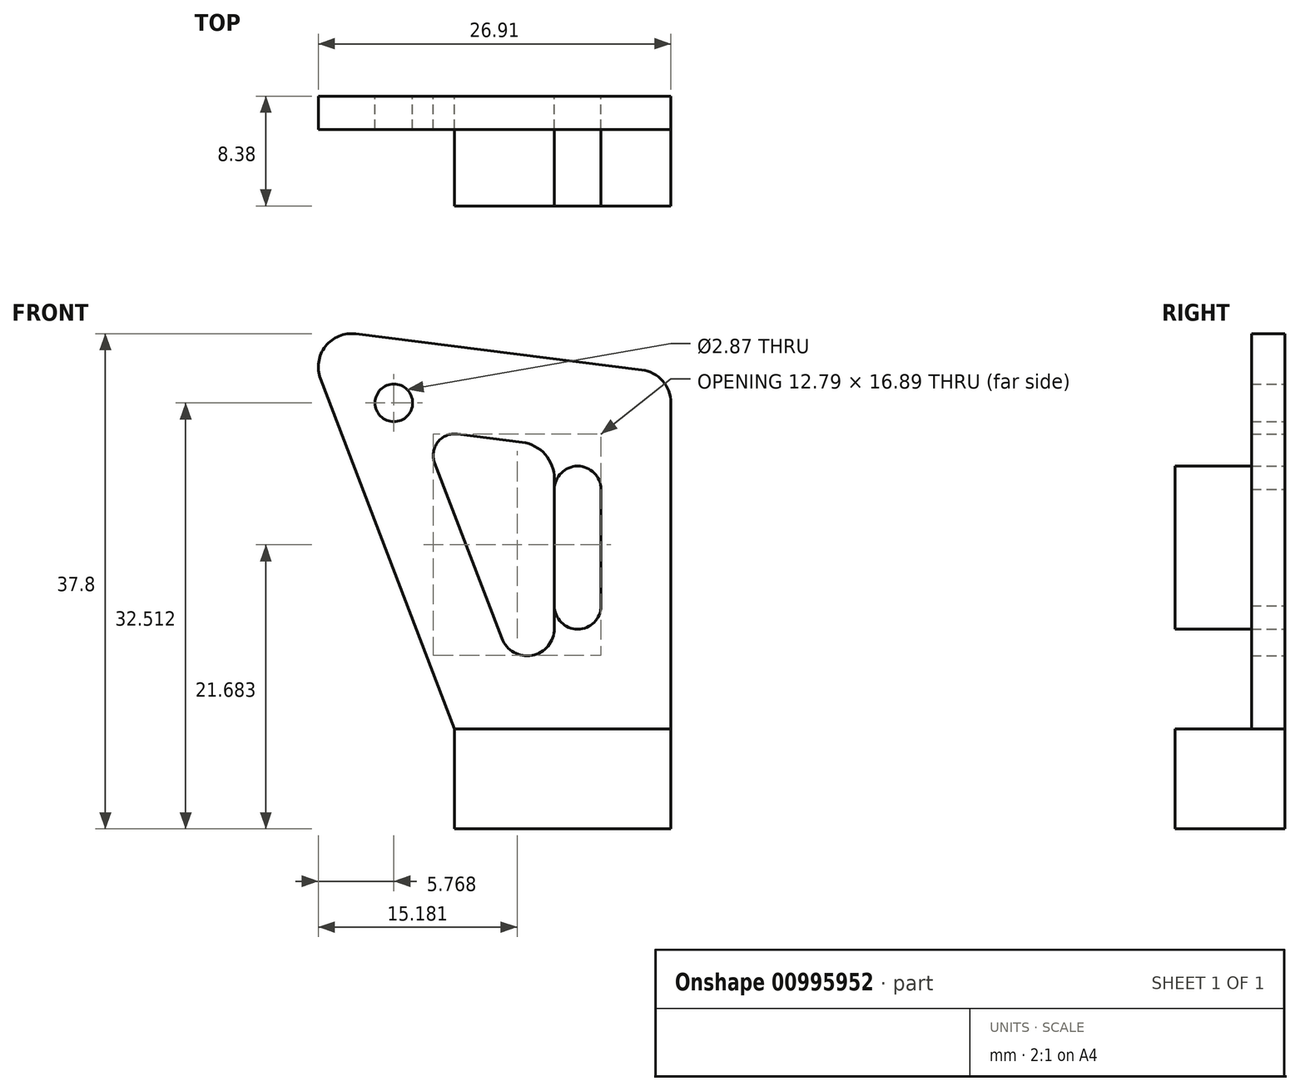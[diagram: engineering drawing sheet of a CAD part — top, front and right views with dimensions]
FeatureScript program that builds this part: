
annotation { "Feature Type Name" : "Feature", "Feature Type Description" : "" }
export const myFeature = defineFeature(function(context is Context, id is Id, definition is map)
    precondition{}
    {
        {
            var Q0;
            Q0=qCreatedBy(makeId("Front.planeOp"),FACE);
            var sketch = newSketch(context, id + "F0", { "sketchPlane" : qUnion([Q0])});
            skLineSegment(sketch, "E0", {"start": v(-2.8, 0.18) * mm, "end": v(-12.25, 24.9) * mm, "construction": true});
            skLineSegment(sketch, "E1", {"start": v(-7.62, 0) * mm, "end": v(8.9, 0) * mm});
            skCircle(sketch, "E2", {"center": v(-12.25, 24.9) * mm, "radius": 1.44 * mm});
            skLineSegment(sketch, "E3", {"start": v(-7.62, 0) * mm, "end": v(-17.85, 26.73) * mm});
            skArc(sketch, "E4", {"start": v(-17.85, 26.73) * mm, "mid": v(-17.48, 29.2) * mm, "end": v(-15.16, 30.16) * mm});
            skLineSegment(sketch, "E5", {"start": v(-15.16, 30.16) * mm, "end": v(6.67, 27.41) * mm});
            skArc(sketch, "E6", {"start": v(6.67, 27.41) * mm, "mid": v(8.25, 26.57) * mm, "end": v(8.89, 24.9) * mm});
            skLineSegment(sketch, "E7", {"start": v(8.9, 0) * mm, "end": v(8.89, 24.9) * mm});
            skLineSegment(sketch, "E8", {"start": v(3.56, 18.29) * mm, "end": v(3.56, 9.4) * mm});
            skLineSegment(sketch, "E9", {"start": v(0, 18.29) * mm, "end": v(0, 9.4) * mm});
            skArc(sketch, "E10", {"start": v(0, 18.29) * mm, "mid": v(1.78, 20.07) * mm, "end": v(3.56, 18.29) * mm});
            skArc(sketch, "E11", {"start": v(0, 9.4) * mm, "mid": v(1.78, 7.62) * mm, "end": v(3.56, 9.4) * mm});
            skLineSegment(sketch, "E12", {"start": v(-4.01, 6.92) * mm, "end": v(-9.14, 20.3) * mm});
            skArc(sketch, "E13", {"start": v(-9.14, 20.3) * mm, "mid": v(-8.9, 21.9) * mm, "end": v(-7.4, 22.51) * mm});
            skLineSegment(sketch, "E14", {"start": v(-7.4, 22.51) * mm, "end": v(-2.47, 21.89) * mm});
            skLineSegment(sketch, "E15", {"start": v(0, 19.1) * mm, "end": v(0, 7.66) * mm});
            skArc(sketch, "E16", {"start": v(-2.47, 21.89) * mm, "mid": v(-0.7, 20.96) * mm, "end": v(0, 19.1) * mm});
            skArc(sketch, "E17", {"start": v(-4.01, 6.92) * mm, "mid": v(-1.7, 5.62) * mm, "end": v(0, 7.66) * mm});
            skLineSegment(sketch, "E18", {"start": v(-17.15, 24.9) * mm, "end": v(8.89, 24.9) * mm, "construction": true});
            skSolve(sketch);
        }
        {
            var Q0;
            Q0=qCreatedBy(makeId("Front.planeOp"),FACE);
            var sketch = newSketch(context, id + "F1", { "sketchPlane" : qUnion([Q0])});
            skLineSegment(sketch, "E19", {"start": v(0, 0) * mm, "end": v(0, -76.2) * mm, "construction": true});
            skLineSegment(sketch, "E20", {"start": v(-12.7, -76.2) * mm, "end": v(12.7, -76.2) * mm});
            skLineSegment(sketch, "E21", {"start": v(-7.62, 0) * mm, "end": v(8.9, 0) * mm});
            skLineSegment(sketch, "E22", {"start": v(-7.62, -7.62) * mm, "end": v(8.9, -7.62) * mm});
            skLineSegment(sketch, "E23", {"start": v(-7.62, 0) * mm, "end": v(-7.62, -7.62) * mm});
            skLineSegment(sketch, "E24", {"start": v(8.9, 0) * mm, "end": v(8.9, -7.62) * mm});
            skLineSegment(sketch, "E25", {"start": v(-7.62, -7.62) * mm, "end": v(-25.4, -63.5) * mm});
            skLineSegment(sketch, "E26", {"start": v(8.89, -7.62) * mm, "end": v(25.4, -63.5) * mm});
            skArc(sketch, "E27", {"start": v(-12.7, -76.2) * mm, "mid": v(-21.68, -72.48) * mm, "end": v(-25.4, -63.5) * mm});
            skArc(sketch, "E28", {"start": v(12.7, -76.2) * mm, "mid": v(21.68, -72.48) * mm, "end": v(25.4, -63.5) * mm});
            skArc(sketch, "E29.0.startCap", {"start": v(-10.16, -68.58) * mm, "mid": v(-16.5, -62.23) * mm, "end": v(-10.16, -55.88) * mm});
            skArc(sketch, "E29.0.endCap", {"start": v(10.16, -55.88) * mm, "mid": v(16.51, -62.23) * mm, "end": v(10.16, -68.58) * mm});
            skLineSegment(sketch, "E29.0.left", {"start": v(-10.16, -55.88) * mm, "end": v(10.16, -55.88) * mm});
            skLineSegment(sketch, "E29.0.right", {"start": v(-10.16, -68.58) * mm, "end": v(10.16, -68.58) * mm});
            skArc(sketch, "E30.0.startCap", {"start": v(-5.08, -48.26) * mm, "mid": v(-11.43, -41.9) * mm, "end": v(-5.08, -35.56) * mm});
            skArc(sketch, "E30.0.endCap", {"start": v(5.08, -35.56) * mm, "mid": v(11.43, -41.9) * mm, "end": v(5.08, -48.26) * mm});
            skLineSegment(sketch, "E30.0.left", {"start": v(-5.08, -35.56) * mm, "end": v(5.08, -35.56) * mm});
            skLineSegment(sketch, "E30.0.right", {"start": v(-5.08, -48.26) * mm, "end": v(5.08, -48.26) * mm});
            skCircle(sketch, "E31", {"center": v(0, -21.59) * mm, "radius": 6.35 * mm});
            skSolve(sketch);
        }
        {
            var Q0;
            Q0=makeQuery(id+"F0.imprint","IMPRINT",FACE,{"disambiguationData":[TD([[makeQuery(id+"F0.imprint","IMPRINT",EDGE,{"derivedFrom":sQuery(id+"F0.wireOp",EDGE,"E1")}),1.0]])]});
            extrude(context, id + "F2", {"entities" : qUnion([Q0]), "depth" : 2.54 * mm, "offsetDistance" : 25.4 * mm});
        }
        {
            var Q0;
            Q0=makeQuery(id+"F0.imprint","IMPRINT",FACE,{"disambiguationData":[TD([[makeQuery(id+"F0.imprint","IMPRINT",EDGE,{"derivedFrom":sQuery(id+"F0.wireOp",EDGE,"E8")}),-1.0]])]});
            var Q1;
            Q1=makeQuery(id+"F1.imprint","IMPRINT",FACE,{"disambiguationData":[TD([[makeQuery(id+"F1.imprint","IMPRINT",EDGE,{"derivedFrom":sQuery(id+"F1.wireOp",EDGE,"E20")}),1.0]])]});
            var Q2;
            Q2=makeQuery(id+"F1.imprint","IMPRINT",FACE,{"disambiguationData":[TD([[makeQuery(id+"F1.imprint","IMPRINT",EDGE,{"derivedFrom":sQuery(id+"F1.wireOp",EDGE,"E21")}),-1.0]])]});
            extrude(context, id + "F3", {"entities" : qUnion([Q0, Q1, Q2]), "depth" : 8.38 * mm, "offsetDistance" : 25.4 * mm});
        }
        {
            var Q0;
            Q0=makeQuery(id+"F0.imprint","IMPRINT",FACE,{"disambiguationData":[TD([[makeQuery(id+"F0.imprint","IMPRINT",EDGE,{"derivedFrom":sQuery(id+"F0.wireOp",EDGE,"E2")}),1.0]])]});
            var Q1;
            Q1=makeQuery(id+"F0.imprint","IMPRINT",FACE,{"disambiguationData":[TD([[makeQuery(id+"F0.imprint","IMPRINT",EDGE,{"derivedFrom":sQuery(id+"F0.wireOp",EDGE,"E12")}),-1.0]])]});
            var Q2;
            Q2=makeQuery(id+"F1.imprint","IMPRINT",FACE,{"disambiguationData":[TD([[makeQuery(id+"F1.imprint","IMPRINT",EDGE,{"derivedFrom":sQuery(id+"F1.wireOp",EDGE,"E31")}),1.0]])]});
            var Q3;
            Q3=makeQuery(id+"F1.imprint","IMPRINT",FACE,{"disambiguationData":[TD([[makeQuery(id+"F1.imprint","IMPRINT",EDGE,{"derivedFrom":sQuery(id+"F1.wireOp",EDGE,"E30.0.startCap")}),-1.0]])]});
            var Q4;
            Q4=makeQuery(id+"F1.imprint","IMPRINT",FACE,{"disambiguationData":[TD([[makeQuery(id+"F1.imprint","IMPRINT",EDGE,{"derivedFrom":sQuery(id+"F1.wireOp",EDGE,"E29.0.startCap")}),-1.0]])]});
            extrude(context, id + "F4", {"entities" : qUnion([Q0, Q1, Q2, Q3, Q4]), "operationType" : NewBodyOperationType.REMOVE, "oppositeDirection" : true, "depth" : 25.4 * mm, "offsetDistance" : 25.4 * mm, "hasSecondDirection" : true, "secondDirectionOppositeDirection" : true, "secondDirectionDepth" : -25.4 * mm});
        }
    });
